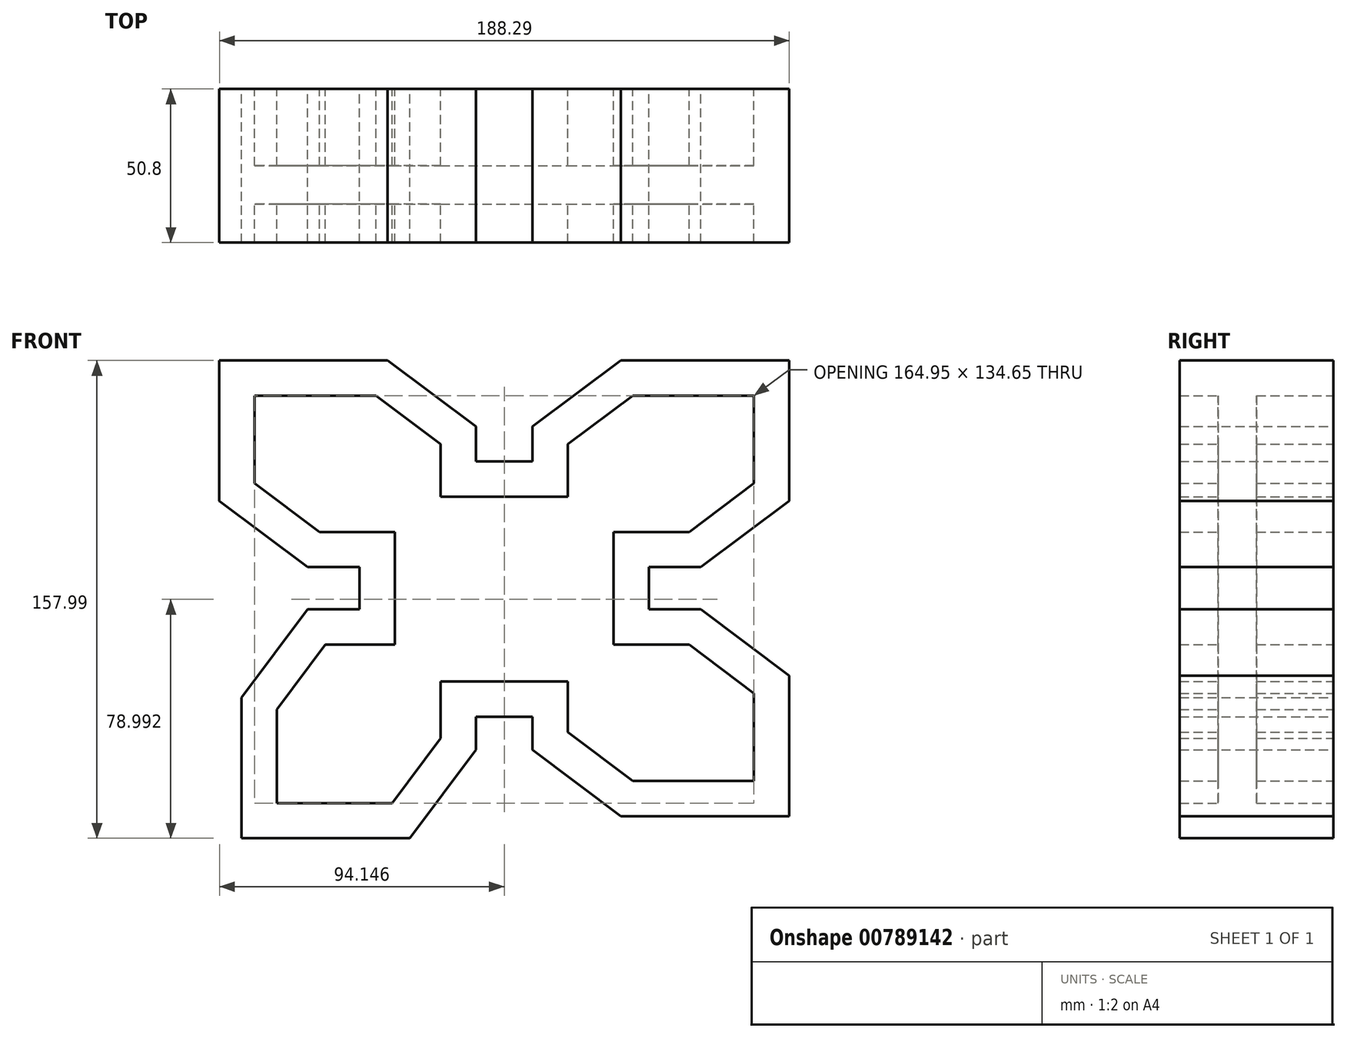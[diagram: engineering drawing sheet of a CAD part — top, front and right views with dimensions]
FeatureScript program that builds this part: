
annotation { "Feature Type Name" : "Feature", "Feature Type Description" : "" }
export const myFeature = defineFeature(function(context is Context, id is Id, definition is map)
    precondition{}
    {
        {
            var Q0;
            Q0=qCreatedBy(makeId("Front.planeOp"),FACE);
            var sketch = newSketch(context, id + "F0", { "sketchPlane" : qUnion([Q0])});
            skLineSegment(sketch, "E0", {"start": v(0, 82.3) * mm, "end": v(0, -102.1) * mm, "construction": true});
            skLineSegment(sketch, "E1", {"start": v(-81.08, 0) * mm, "end": v(88.5, 0) * mm, "construction": true});
            skLineSegment(sketch, "E2", {"start": v(-3.62, 49) * mm, "end": v(15.07, 49) * mm});
            skLineSegment(sketch, "E3", {"start": v(15.07, 49) * mm, "end": v(15.07, 60.45) * mm});
            skLineSegment(sketch, "E4", {"start": v(15.07, 60.45) * mm, "end": v(44.27, 82.3) * mm});
            skLineSegment(sketch, "E5", {"start": v(44.27, 82.3) * mm, "end": v(99.87, 82.3) * mm});
            skLineSegment(sketch, "E6", {"start": v(99.87, 82.3) * mm, "end": v(99.87, 35.83) * mm});
            skLineSegment(sketch, "E7", {"start": v(-3.62, 60.45) * mm, "end": v(-3.62, 49) * mm});
            skLineSegment(sketch, "E8", {"start": v(-3.62, 60.45) * mm, "end": v(-32.82, 82.3) * mm});
            skLineSegment(sketch, "E9", {"start": v(-32.82, 82.3) * mm, "end": v(-88.42, 82.3) * mm});
            skLineSegment(sketch, "E10", {"start": v(-88.42, 82.3) * mm, "end": v(-88.42, 35.83) * mm});
            skLineSegment(sketch, "E11", {"start": v(-88.42, 35.83) * mm, "end": v(-59.22, 13.97) * mm});
            skLineSegment(sketch, "E12", {"start": v(-59.22, 13.97) * mm, "end": v(-42.1, 13.97) * mm});
            skLineSegment(sketch, "E13", {"start": v(-42.1, 13.97) * mm, "end": v(-42.1, 0) * mm});
            skLineSegment(sketch, "E14", {"start": v(-42.1, 0) * mm, "end": v(-59.22, 0) * mm});
            skLineSegment(sketch, "E15", {"start": v(-59.22, 0) * mm, "end": v(-81.08, -29.2) * mm});
            skLineSegment(sketch, "E16", {"start": v(-81.08, -29.2) * mm, "end": v(-81.08, -75.68) * mm});
            skLineSegment(sketch, "E17", {"start": v(-81.08, -75.68) * mm, "end": v(-25.48, -75.68) * mm});
            skLineSegment(sketch, "E18", {"start": v(-25.48, -75.68) * mm, "end": v(-3.62, -46.48) * mm});
            skLineSegment(sketch, "E19", {"start": v(-3.62, -46.48) * mm, "end": v(-3.62, -35.53) * mm});
            skLineSegment(sketch, "E20", {"start": v(-3.62, -35.53) * mm, "end": v(15.07, -35.53) * mm});
            skLineSegment(sketch, "E21", {"start": v(15.07, -35.53) * mm, "end": v(15.07, -46.48) * mm});
            skLineSegment(sketch, "E22", {"start": v(15.07, -46.48) * mm, "end": v(44.27, -68.34) * mm});
            skLineSegment(sketch, "E23", {"start": v(99.87, -68.34) * mm, "end": v(44.27, -68.34) * mm});
            skLineSegment(sketch, "E24", {"start": v(99.87, -68.34) * mm, "end": v(99.87, -21.86) * mm});
            skLineSegment(sketch, "E25", {"start": v(99.87, -21.86) * mm, "end": v(70.67, 0) * mm});
            skLineSegment(sketch, "E26", {"start": v(70.67, 0) * mm, "end": v(53.54, 0) * mm});
            skLineSegment(sketch, "E27", {"start": v(53.54, 0) * mm, "end": v(53.54, 13.97) * mm});
            skLineSegment(sketch, "E28", {"start": v(53.54, 13.97) * mm, "end": v(70.67, 13.97) * mm});
            skLineSegment(sketch, "E29", {"start": v(70.67, 13.97) * mm, "end": v(99.87, 35.83) * mm});
            skLineSegment(sketch, "E30.0", {"start": v(-30.43, -11.67) * mm, "end": v(-53.38, -11.67) * mm});
            skLineSegment(sketch, "E30.1", {"start": v(-30.43, 25.64) * mm, "end": v(-30.43, -11.67) * mm});
            skLineSegment(sketch, "E30.2", {"start": v(-55.34, 25.64) * mm, "end": v(-30.43, 25.64) * mm});
            skLineSegment(sketch, "E30.3", {"start": v(-76.75, 41.67) * mm, "end": v(-55.34, 25.64) * mm});
            skLineSegment(sketch, "E30.4", {"start": v(-76.75, 70.64) * mm, "end": v(-76.75, 41.67) * mm});
            skLineSegment(sketch, "E30.5", {"start": v(88.2, -27.7) * mm, "end": v(66.79, -11.67) * mm});
            skLineSegment(sketch, "E30.6", {"start": v(88.2, -56.67) * mm, "end": v(88.2, -27.7) * mm});
            skLineSegment(sketch, "E30.7", {"start": v(88.2, -56.67) * mm, "end": v(48.16, -56.67) * mm});
            skLineSegment(sketch, "E30.8", {"start": v(26.74, -40.64) * mm, "end": v(48.16, -56.67) * mm});
            skLineSegment(sketch, "E30.9", {"start": v(26.74, -23.86) * mm, "end": v(26.74, -40.64) * mm});
            skLineSegment(sketch, "E30.10", {"start": v(-15.3, -23.86) * mm, "end": v(26.74, -23.86) * mm});
            skLineSegment(sketch, "E30.11", {"start": v(-69.4, -33.09) * mm, "end": v(-69.4, -64.01) * mm});
            skLineSegment(sketch, "E30.12", {"start": v(-69.4, -64.01) * mm, "end": v(-31.32, -64.01) * mm});
            skLineSegment(sketch, "E30.13", {"start": v(-31.32, -64.01) * mm, "end": v(-15.3, -42.6) * mm});
            skLineSegment(sketch, "E30.14", {"start": v(-15.3, -42.6) * mm, "end": v(-15.3, -23.86) * mm});
            skLineSegment(sketch, "E30.15", {"start": v(66.79, -11.67) * mm, "end": v(41.87, -11.67) * mm});
            skLineSegment(sketch, "E30.16", {"start": v(41.87, -11.67) * mm, "end": v(41.87, 25.64) * mm});
            skLineSegment(sketch, "E30.17", {"start": v(41.87, 25.64) * mm, "end": v(66.79, 25.64) * mm});
            skLineSegment(sketch, "E30.18", {"start": v(66.79, 25.64) * mm, "end": v(88.2, 41.67) * mm});
            skLineSegment(sketch, "E30.19", {"start": v(88.2, 70.64) * mm, "end": v(88.2, 41.67) * mm});
            skLineSegment(sketch, "E30.20", {"start": v(-53.38, -11.67) * mm, "end": v(-69.4, -33.09) * mm});
            skLineSegment(sketch, "E30.21", {"start": v(48.16, 70.64) * mm, "end": v(88.2, 70.64) * mm});
            skLineSegment(sketch, "E30.22", {"start": v(26.75, 54.6) * mm, "end": v(48.16, 70.64) * mm});
            skLineSegment(sketch, "E30.23", {"start": v(26.75, 37.33) * mm, "end": v(26.75, 54.6) * mm});
            skLineSegment(sketch, "E30.24", {"start": v(-15.3, 37.33) * mm, "end": v(26.75, 37.33) * mm});
            skLineSegment(sketch, "E30.25", {"start": v(-15.3, 54.6) * mm, "end": v(-15.3, 37.33) * mm});
            skLineSegment(sketch, "E30.26", {"start": v(-15.3, 54.6) * mm, "end": v(-36.7, 70.64) * mm});
            skLineSegment(sketch, "E30.27", {"start": v(-36.7, 70.64) * mm, "end": v(-76.75, 70.64) * mm});
            skSolve(sketch);
        }
        {
            var Q0;
            Q0=makeQuery(id+"F0.imprint","IMPRINT",FACE,{"disambiguationData":[TD([[makeQuery(id+"F0.imprint","IMPRINT",EDGE,{"derivedFrom":sQuery(id+"F0.wireOp",EDGE,"E30.0")}),1.0]])]});
            extrude(context, id + "F1", {"entities" : qUnion([Q0]), "depth" : 12.7 * mm, "offsetDistance" : 25.4 * mm});
        }
        {
            var Q0;
            Q0=makeQuery(id+"F0.imprint","IMPRINT",FACE,{"disambiguationData":[TD([[makeQuery(id+"F0.imprint","IMPRINT",EDGE,{"derivedFrom":sQuery(id+"F0.wireOp",EDGE,"E2")}),-1.0]])]});
            extrude(context, id + "F2", {"entities" : qUnion([Q0]), "operationType" : NewBodyOperationType.ADD, "endBound" : BoundingType.SYMMETRIC, "depth" : 50.8 * mm, "offsetDistance" : 25.4 * mm});
        }
    });
